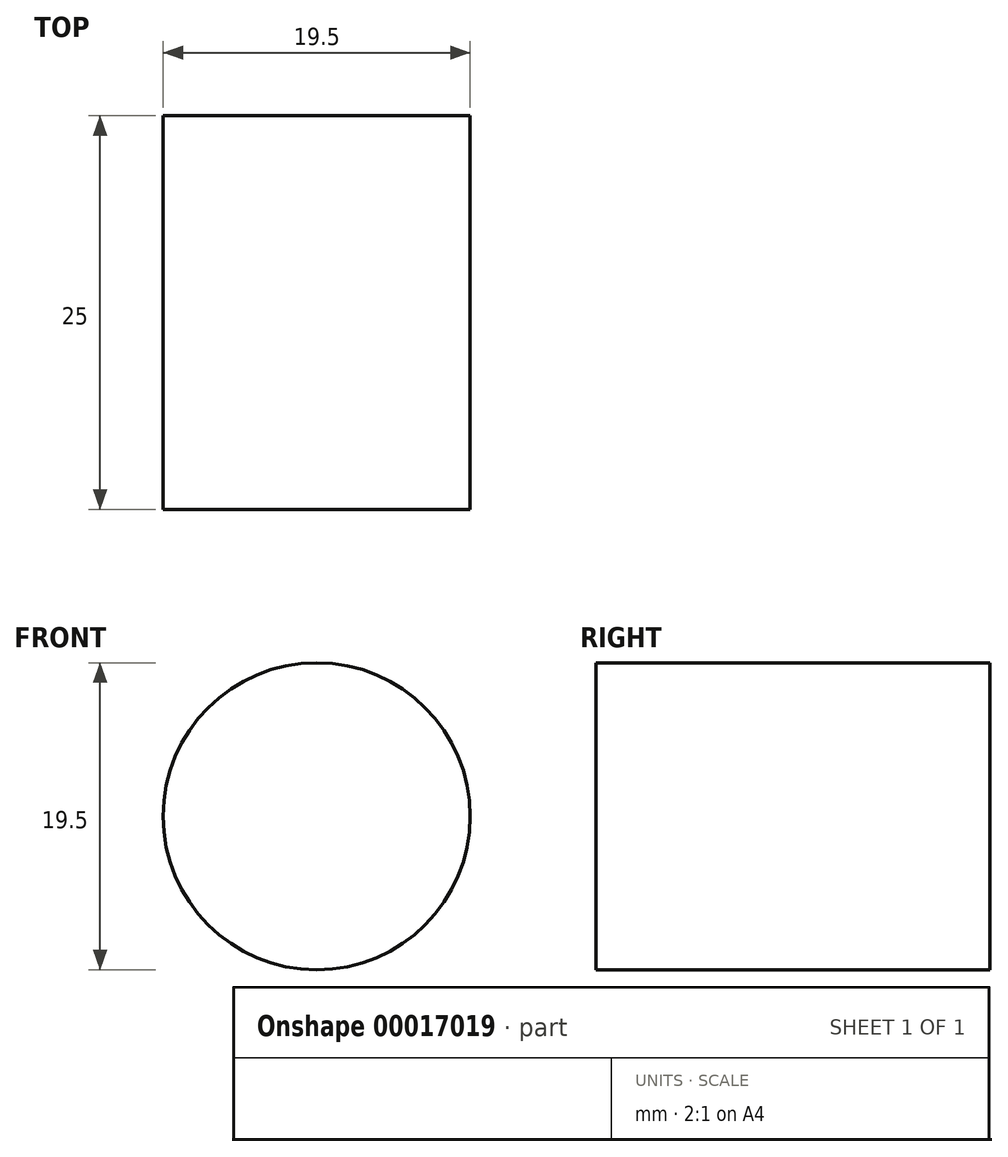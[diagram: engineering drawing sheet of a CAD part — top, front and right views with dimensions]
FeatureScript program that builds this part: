
annotation { "Feature Type Name" : "Feature", "Feature Type Description" : "" }
export const myFeature = defineFeature(function(context is Context, id is Id, definition is map)
    precondition{}
    {
        {
            var Q0;
            Q0=qCreatedBy(makeId("Front.planeOp"),FACE);
            var sketch = newSketch(context, id + "F0", { "sketchPlane" : qUnion([Q0])});
            skCircle(sketch, "E0", {"center": v(0, 0) * mm, "radius": 9.75 * mm});
            skSolve(sketch);
        }
        {
            var Q0;
            Q0 = qSketchRegion(id + "F0", true);
            extrude(context, id + "F1", {"entities" : qUnion([Q0]), "depth" : 25 * mm});
        }
    });
